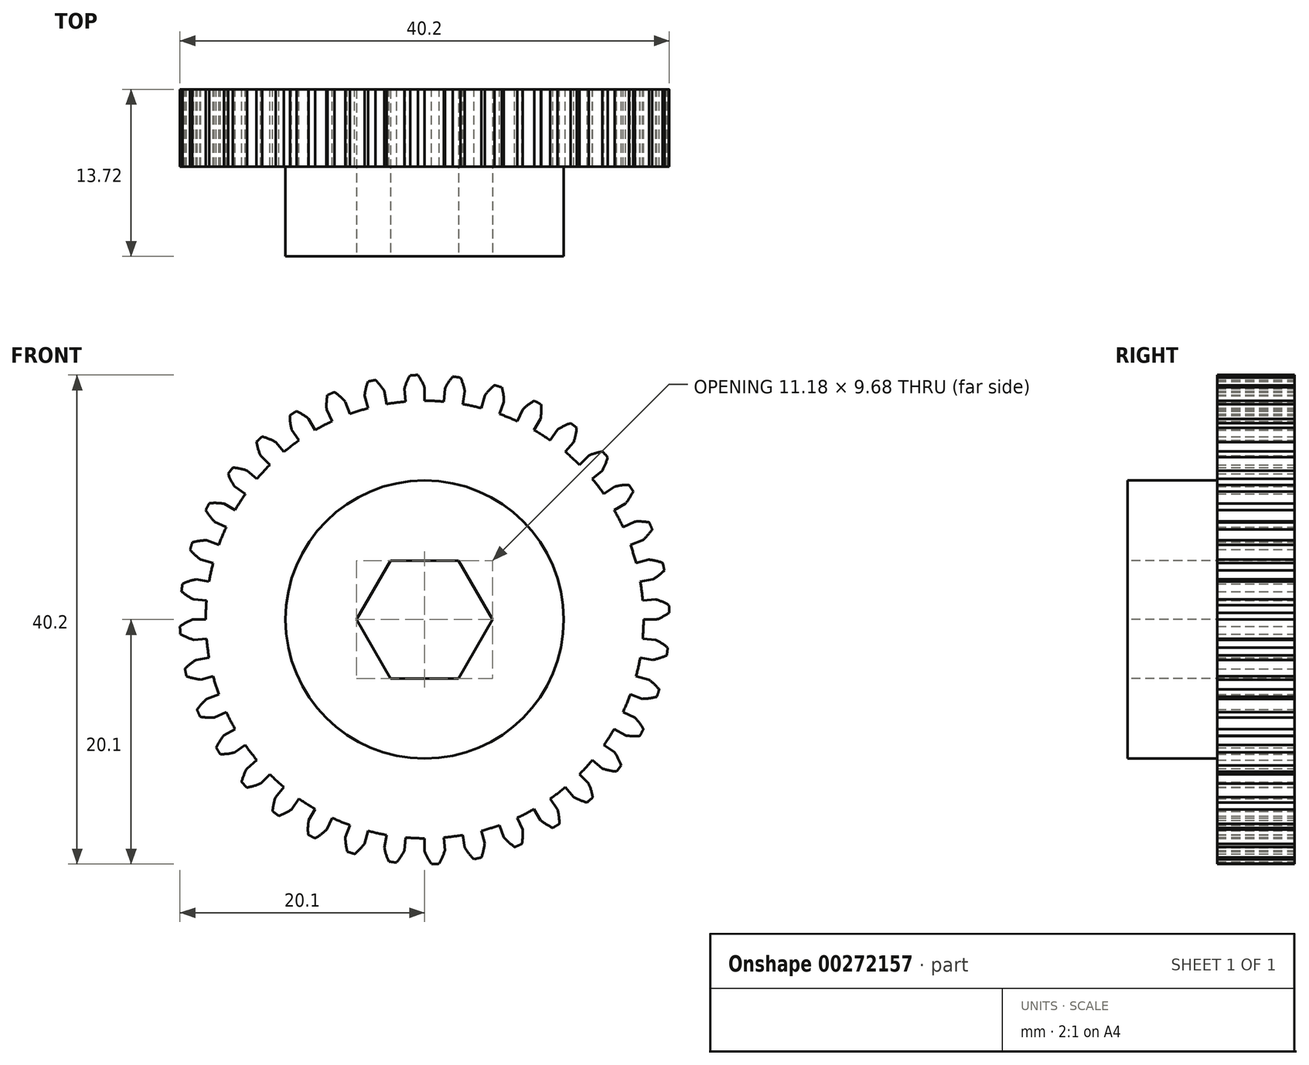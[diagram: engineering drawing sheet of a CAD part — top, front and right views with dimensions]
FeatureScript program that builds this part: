
annotation { "Feature Type Name" : "Feature", "Feature Type Description" : "" }
export const myFeature = defineFeature(function(context is Context, id is Id, definition is map)
    precondition{}
    {
        {
            var Q0;
            Q0=qCreatedBy(makeId("Front.planeOp"),FACE);
            var sketch = newSketch(context, id + "F0", { "sketchPlane" : qUnion([Q0])});
            skArc(sketch, "E0", {"start": v(4.65, 17.37) * mm, "mid": v(-6.88, -16.61) * mm, "end": v(9, 15.57) * mm});
            skLineSegment(sketch, "E1", {"start": v(0, 17.98) * mm, "end": v(0, 19.05) * mm});
            skLineSegment(sketch, "E2", {"start": v(0, 0) * mm, "end": v(-0.88, 20.08) * mm, "construction": true});
            skArc(sketch, "E3.trimOffspring", {"start": v(-0.56, 20.1) * mm, "mid": v(-0.72, 20.1) * mm, "end": v(-0.88, 20.08) * mm});
            skArc(sketch, "E4.trimOffspring", {"start": v(0, 19.05) * mm, "mid": v(-0.25, 19.6) * mm, "end": v(-0.56, 20.1) * mm});
            skLineSegment(sketch, "E5.MirrorCS", {"start": v(-1.57, 17.91) * mm, "end": v(-1.66, 18.98) * mm});
            skArc(sketch, "E6.MirrorCS", {"start": v(-1.66, 18.98) * mm, "mid": v(-1.46, 19.54) * mm, "end": v(-1.2, 20.07) * mm});
            skArc(sketch, "E7.MirrorCS", {"start": v(-1.2, 20.07) * mm, "mid": v(-1.03, 20.08) * mm, "end": v(-0.88, 20.08) * mm});
            skLineSegment(sketch, "E8.1.0", {"start": v(-4.65, 17.37) * mm, "end": v(-4.93, 18.4) * mm});
            skArc(sketch, "E8.1.1", {"start": v(-3.3, 18.76) * mm, "mid": v(-3.65, 19.25) * mm, "end": v(-4.04, 19.7) * mm});
            skLineSegment(sketch, "E8.1.2", {"start": v(-3.12, 17.7) * mm, "end": v(-3.3, 18.76) * mm});
            skArc(sketch, "E8.1.3", {"start": v(-4.93, 18.4) * mm, "mid": v(-4.83, 18.99) * mm, "end": v(-4.66, 19.56) * mm});
            skArc(sketch, "E8.1.4", {"start": v(-4.66, 19.56) * mm, "mid": v(-4.5, 19.6) * mm, "end": v(-4.35, 19.63) * mm});
            skArc(sketch, "E8.1.5", {"start": v(-4.04, 19.7) * mm, "mid": v(-4.2, 19.66) * mm, "end": v(-4.35, 19.63) * mm});
            skLineSegment(sketch, "E8.2.0", {"start": v(-7.6, 16.3) * mm, "end": v(-8.05, 17.27) * mm});
            skArc(sketch, "E8.2.1", {"start": v(-6.52, 17.9) * mm, "mid": v(-6.93, 18.32) * mm, "end": v(-7.4, 18.7) * mm});
            skLineSegment(sketch, "E8.2.2", {"start": v(-6.15, 16.9) * mm, "end": v(-6.52, 17.9) * mm});
            skArc(sketch, "E8.2.3", {"start": v(-8.05, 17.27) * mm, "mid": v(-8.05, 17.86) * mm, "end": v(-7.98, 18.45) * mm});
            skArc(sketch, "E8.2.4", {"start": v(-7.98, 18.45) * mm, "mid": v(-7.84, 18.51) * mm, "end": v(-7.7, 18.57) * mm});
            skArc(sketch, "E8.2.5", {"start": v(-7.4, 18.7) * mm, "mid": v(-7.55, 18.63) * mm, "end": v(-7.7, 18.57) * mm});
            skLineSegment(sketch, "E8.3.0", {"start": v(-10.31, 14.73) * mm, "end": v(-10.93, 15.6) * mm});
            skArc(sketch, "E8.3.1", {"start": v(-9.52, 16.5) * mm, "mid": v(-10, 16.84) * mm, "end": v(-10.53, 17.12) * mm});
            skLineSegment(sketch, "E8.3.2", {"start": v(-9, 15.57) * mm, "end": v(-9.52, 16.5) * mm});
            skArc(sketch, "E8.3.3", {"start": v(-10.93, 15.6) * mm, "mid": v(-11.03, 16.19) * mm, "end": v(-11.07, 16.78) * mm});
            skArc(sketch, "E8.3.4", {"start": v(-11.07, 16.78) * mm, "mid": v(-10.93, 16.87) * mm, "end": v(-10.8, 16.96) * mm});
            skArc(sketch, "E8.3.5", {"start": v(-10.53, 17.12) * mm, "mid": v(-10.67, 17.04) * mm, "end": v(-10.8, 16.96) * mm});
            skLineSegment(sketch, "E8.4.0", {"start": v(-12.72, 12.72) * mm, "end": v(-13.47, 13.47) * mm});
            skArc(sketch, "E8.4.1", {"start": v(-12.25, 14.6) * mm, "mid": v(-12.78, 14.85) * mm, "end": v(-13.35, 15.03) * mm});
            skLineSegment(sketch, "E8.4.2", {"start": v(-11.56, 13.78) * mm, "end": v(-12.25, 14.6) * mm});
            skArc(sketch, "E8.4.3", {"start": v(-13.47, 13.47) * mm, "mid": v(-13.68, 14.03) * mm, "end": v(-13.81, 14.6) * mm});
            skArc(sketch, "E8.4.4", {"start": v(-13.81, 14.6) * mm, "mid": v(-13.7, 14.72) * mm, "end": v(-13.58, 14.82) * mm});
            skArc(sketch, "E8.4.5", {"start": v(-13.35, 15.03) * mm, "mid": v(-13.47, 14.93) * mm, "end": v(-13.58, 14.82) * mm});
            skLineSegment(sketch, "E8.5.0", {"start": v(-14.73, 10.31) * mm, "end": v(-15.6, 10.93) * mm});
            skArc(sketch, "E8.5.1", {"start": v(-14.6, 12.25) * mm, "mid": v(-15.17, 12.4) * mm, "end": v(-15.76, 12.49) * mm});
            skLineSegment(sketch, "E8.5.2", {"start": v(-13.78, 11.56) * mm, "end": v(-14.6, 12.25) * mm});
            skArc(sketch, "E8.5.3", {"start": v(-15.6, 10.93) * mm, "mid": v(-15.9, 11.44) * mm, "end": v(-16.14, 11.99) * mm});
            skArc(sketch, "E8.5.4", {"start": v(-16.14, 11.99) * mm, "mid": v(-16.05, 12.11) * mm, "end": v(-15.95, 12.24) * mm});
            skArc(sketch, "E8.5.5", {"start": v(-15.76, 12.49) * mm, "mid": v(-15.85, 12.36) * mm, "end": v(-15.95, 12.24) * mm});
            skLineSegment(sketch, "E8.6.0", {"start": v(-16.3, 7.6) * mm, "end": v(-17.27, 8.05) * mm});
            skArc(sketch, "E8.6.1", {"start": v(-16.5, 9.53) * mm, "mid": v(-17.09, 9.58) * mm, "end": v(-17.68, 9.56) * mm});
            skLineSegment(sketch, "E8.6.2", {"start": v(-15.57, 9) * mm, "end": v(-16.5, 9.53) * mm});
            skArc(sketch, "E8.6.3", {"start": v(-17.27, 8.05) * mm, "mid": v(-17.65, 8.5) * mm, "end": v(-17.98, 9) * mm});
            skArc(sketch, "E8.6.4", {"start": v(-17.98, 9) * mm, "mid": v(-17.9, 9.14) * mm, "end": v(-17.83, 9.28) * mm});
            skArc(sketch, "E8.6.5", {"start": v(-17.68, 9.56) * mm, "mid": v(-17.76, 9.42) * mm, "end": v(-17.83, 9.28) * mm});
            skLineSegment(sketch, "E8.7.0", {"start": v(-17.37, 4.65) * mm, "end": v(-18.4, 4.93) * mm});
            skArc(sketch, "E8.7.1", {"start": v(-17.9, 6.52) * mm, "mid": v(-18.5, 6.47) * mm, "end": v(-19.08, 6.35) * mm});
            skLineSegment(sketch, "E8.7.2", {"start": v(-16.9, 6.15) * mm, "end": v(-17.9, 6.52) * mm});
            skArc(sketch, "E8.7.3", {"start": v(-18.4, 4.93) * mm, "mid": v(-18.86, 5.3) * mm, "end": v(-19.27, 5.74) * mm});
            skArc(sketch, "E8.7.4", {"start": v(-19.27, 5.74) * mm, "mid": v(-19.22, 5.9) * mm, "end": v(-19.17, 6.05) * mm});
            skArc(sketch, "E8.7.5", {"start": v(-19.08, 6.35) * mm, "mid": v(-19.13, 6.2) * mm, "end": v(-19.17, 6.05) * mm});
            skLineSegment(sketch, "E8.8.0", {"start": v(-17.91, 1.57) * mm, "end": v(-18.98, 1.66) * mm});
            skArc(sketch, "E8.8.1", {"start": v(-18.76, 3.3) * mm, "mid": v(-19.34, 3.16) * mm, "end": v(-19.89, 2.94) * mm});
            skLineSegment(sketch, "E8.8.2", {"start": v(-17.7, 3.12) * mm, "end": v(-18.76, 3.3) * mm});
            skArc(sketch, "E8.8.3", {"start": v(-18.98, 1.66) * mm, "mid": v(-19.5, 1.95) * mm, "end": v(-19.97, 2.31) * mm});
            skArc(sketch, "E8.8.4", {"start": v(-19.97, 2.31) * mm, "mid": v(-19.95, 2.47) * mm, "end": v(-19.93, 2.62) * mm});
            skArc(sketch, "E8.8.5", {"start": v(-19.89, 2.94) * mm, "mid": v(-19.91, 2.78) * mm, "end": v(-19.93, 2.62) * mm});
            skLineSegment(sketch, "E8.9.0", {"start": v(-17.91, -1.57) * mm, "end": v(-18.98, -1.66) * mm});
            skArc(sketch, "E8.9.1", {"start": v(-19.05, 0) * mm, "mid": v(-19.6, -0.25) * mm, "end": v(-20.1, -0.56) * mm});
            skLineSegment(sketch, "E8.9.2", {"start": v(-17.98, 0) * mm, "end": v(-19.05, 0) * mm});
            skArc(sketch, "E8.9.3", {"start": v(-18.98, -1.66) * mm, "mid": v(-19.54, -1.46) * mm, "end": v(-20.07, -1.2) * mm});
            skArc(sketch, "E8.9.4", {"start": v(-20.07, -1.2) * mm, "mid": v(-20.08, -1.03) * mm, "end": v(-20.08, -0.88) * mm});
            skArc(sketch, "E8.9.5", {"start": v(-20.1, -0.56) * mm, "mid": v(-20.1, -0.72) * mm, "end": v(-20.08, -0.88) * mm});
            skLineSegment(sketch, "E8.10.0", {"start": v(-17.37, -4.65) * mm, "end": v(-18.4, -4.93) * mm});
            skArc(sketch, "E8.10.1", {"start": v(-18.76, -3.3) * mm, "mid": v(-19.25, -3.65) * mm, "end": v(-19.7, -4.04) * mm});
            skLineSegment(sketch, "E8.10.2", {"start": v(-17.7, -3.12) * mm, "end": v(-18.76, -3.3) * mm});
            skArc(sketch, "E8.10.3", {"start": v(-18.4, -4.93) * mm, "mid": v(-18.99, -4.83) * mm, "end": v(-19.56, -4.66) * mm});
            skArc(sketch, "E8.10.4", {"start": v(-19.56, -4.66) * mm, "mid": v(-19.6, -4.5) * mm, "end": v(-19.63, -4.35) * mm});
            skArc(sketch, "E8.10.5", {"start": v(-19.7, -4.04) * mm, "mid": v(-19.66, -4.2) * mm, "end": v(-19.63, -4.35) * mm});
            skLineSegment(sketch, "E8.11.0", {"start": v(-16.3, -7.6) * mm, "end": v(-17.27, -8.05) * mm});
            skArc(sketch, "E8.11.1", {"start": v(-17.9, -6.52) * mm, "mid": v(-18.32, -6.93) * mm, "end": v(-18.7, -7.4) * mm});
            skLineSegment(sketch, "E8.11.2", {"start": v(-16.9, -6.15) * mm, "end": v(-17.9, -6.52) * mm});
            skArc(sketch, "E8.11.3", {"start": v(-17.27, -8.05) * mm, "mid": v(-17.86, -8.05) * mm, "end": v(-18.45, -7.98) * mm});
            skArc(sketch, "E8.11.4", {"start": v(-18.45, -7.98) * mm, "mid": v(-18.51, -7.84) * mm, "end": v(-18.57, -7.7) * mm});
            skArc(sketch, "E8.11.5", {"start": v(-18.7, -7.4) * mm, "mid": v(-18.63, -7.55) * mm, "end": v(-18.57, -7.7) * mm});
            skLineSegment(sketch, "E8.12.0", {"start": v(-14.73, -10.31) * mm, "end": v(-15.6, -10.93) * mm});
            skArc(sketch, "E8.12.1", {"start": v(-16.5, -9.52) * mm, "mid": v(-16.84, -10) * mm, "end": v(-17.12, -10.53) * mm});
            skLineSegment(sketch, "E8.12.2", {"start": v(-15.57, -9) * mm, "end": v(-16.5, -9.52) * mm});
            skArc(sketch, "E8.12.3", {"start": v(-15.6, -10.93) * mm, "mid": v(-16.19, -11.03) * mm, "end": v(-16.78, -11.07) * mm});
            skArc(sketch, "E8.12.4", {"start": v(-16.78, -11.07) * mm, "mid": v(-16.87, -10.93) * mm, "end": v(-16.96, -10.8) * mm});
            skArc(sketch, "E8.12.5", {"start": v(-17.12, -10.53) * mm, "mid": v(-17.04, -10.67) * mm, "end": v(-16.96, -10.8) * mm});
            skLineSegment(sketch, "E8.13.0", {"start": v(-12.72, -12.72) * mm, "end": v(-13.47, -13.47) * mm});
            skArc(sketch, "E8.13.1", {"start": v(-14.6, -12.25) * mm, "mid": v(-14.85, -12.78) * mm, "end": v(-15.03, -13.35) * mm});
            skLineSegment(sketch, "E8.13.2", {"start": v(-13.78, -11.56) * mm, "end": v(-14.6, -12.25) * mm});
            skArc(sketch, "E8.13.3", {"start": v(-13.47, -13.47) * mm, "mid": v(-14.03, -13.68) * mm, "end": v(-14.6, -13.81) * mm});
            skArc(sketch, "E8.13.4", {"start": v(-14.6, -13.81) * mm, "mid": v(-14.72, -13.7) * mm, "end": v(-14.82, -13.58) * mm});
            skArc(sketch, "E8.13.5", {"start": v(-15.03, -13.35) * mm, "mid": v(-14.93, -13.47) * mm, "end": v(-14.82, -13.58) * mm});
            skLineSegment(sketch, "E8.14.0", {"start": v(-10.31, -14.73) * mm, "end": v(-10.93, -15.6) * mm});
            skArc(sketch, "E8.14.1", {"start": v(-12.25, -14.6) * mm, "mid": v(-12.4, -15.17) * mm, "end": v(-12.49, -15.76) * mm});
            skLineSegment(sketch, "E8.14.2", {"start": v(-11.56, -13.78) * mm, "end": v(-12.25, -14.6) * mm});
            skArc(sketch, "E8.14.3", {"start": v(-10.93, -15.6) * mm, "mid": v(-11.44, -15.9) * mm, "end": v(-11.99, -16.14) * mm});
            skArc(sketch, "E8.14.4", {"start": v(-11.99, -16.14) * mm, "mid": v(-12.11, -16.05) * mm, "end": v(-12.24, -15.95) * mm});
            skArc(sketch, "E8.14.5", {"start": v(-12.49, -15.76) * mm, "mid": v(-12.36, -15.85) * mm, "end": v(-12.24, -15.95) * mm});
            skLineSegment(sketch, "E8.15.0", {"start": v(-7.6, -16.3) * mm, "end": v(-8.05, -17.27) * mm});
            skArc(sketch, "E8.15.1", {"start": v(-9.53, -16.5) * mm, "mid": v(-9.58, -17.09) * mm, "end": v(-9.56, -17.68) * mm});
            skLineSegment(sketch, "E8.15.2", {"start": v(-9, -15.57) * mm, "end": v(-9.53, -16.5) * mm});
            skArc(sketch, "E8.15.3", {"start": v(-8.05, -17.27) * mm, "mid": v(-8.5, -17.65) * mm, "end": v(-9, -17.98) * mm});
            skArc(sketch, "E8.15.4", {"start": v(-9, -17.98) * mm, "mid": v(-9.14, -17.9) * mm, "end": v(-9.28, -17.83) * mm});
            skArc(sketch, "E8.15.5", {"start": v(-9.56, -17.68) * mm, "mid": v(-9.42, -17.76) * mm, "end": v(-9.28, -17.83) * mm});
            skLineSegment(sketch, "E8.16.0", {"start": v(-4.65, -17.37) * mm, "end": v(-4.93, -18.4) * mm});
            skArc(sketch, "E8.16.1", {"start": v(-6.52, -17.9) * mm, "mid": v(-6.47, -18.5) * mm, "end": v(-6.35, -19.08) * mm});
            skLineSegment(sketch, "E8.16.2", {"start": v(-6.15, -16.9) * mm, "end": v(-6.52, -17.9) * mm});
            skArc(sketch, "E8.16.3", {"start": v(-4.93, -18.4) * mm, "mid": v(-5.3, -18.86) * mm, "end": v(-5.74, -19.27) * mm});
            skArc(sketch, "E8.16.4", {"start": v(-5.74, -19.27) * mm, "mid": v(-5.9, -19.22) * mm, "end": v(-6.05, -19.17) * mm});
            skArc(sketch, "E8.16.5", {"start": v(-6.35, -19.08) * mm, "mid": v(-6.2, -19.13) * mm, "end": v(-6.05, -19.17) * mm});
            skLineSegment(sketch, "E8.17.0", {"start": v(-1.57, -17.91) * mm, "end": v(-1.66, -18.98) * mm});
            skArc(sketch, "E8.17.1", {"start": v(-3.3, -18.76) * mm, "mid": v(-3.16, -19.34) * mm, "end": v(-2.94, -19.89) * mm});
            skLineSegment(sketch, "E8.17.2", {"start": v(-3.12, -17.7) * mm, "end": v(-3.3, -18.76) * mm});
            skArc(sketch, "E8.17.3", {"start": v(-1.66, -18.98) * mm, "mid": v(-1.95, -19.5) * mm, "end": v(-2.31, -19.97) * mm});
            skArc(sketch, "E8.17.4", {"start": v(-2.31, -19.97) * mm, "mid": v(-2.47, -19.95) * mm, "end": v(-2.62, -19.93) * mm});
            skArc(sketch, "E8.17.5", {"start": v(-2.94, -19.89) * mm, "mid": v(-2.78, -19.91) * mm, "end": v(-2.62, -19.93) * mm});
            skLineSegment(sketch, "E8.18.0", {"start": v(1.57, -17.91) * mm, "end": v(1.66, -18.98) * mm});
            skArc(sketch, "E8.18.1", {"start": v(0, -19.05) * mm, "mid": v(0.25, -19.6) * mm, "end": v(0.56, -20.1) * mm});
            skLineSegment(sketch, "E8.18.2", {"start": v(0, -17.98) * mm, "end": v(0, -19.05) * mm});
            skArc(sketch, "E8.18.3", {"start": v(1.66, -18.98) * mm, "mid": v(1.46, -19.54) * mm, "end": v(1.2, -20.07) * mm});
            skArc(sketch, "E8.18.4", {"start": v(1.2, -20.07) * mm, "mid": v(1.03, -20.08) * mm, "end": v(0.88, -20.08) * mm});
            skArc(sketch, "E8.18.5", {"start": v(0.56, -20.1) * mm, "mid": v(0.72, -20.1) * mm, "end": v(0.88, -20.08) * mm});
            skLineSegment(sketch, "E8.19.0", {"start": v(4.65, -17.37) * mm, "end": v(4.93, -18.4) * mm});
            skArc(sketch, "E8.19.1", {"start": v(3.3, -18.76) * mm, "mid": v(3.65, -19.25) * mm, "end": v(4.04, -19.7) * mm});
            skLineSegment(sketch, "E8.19.2", {"start": v(3.12, -17.7) * mm, "end": v(3.3, -18.76) * mm});
            skArc(sketch, "E8.19.3", {"start": v(4.93, -18.4) * mm, "mid": v(4.83, -18.99) * mm, "end": v(4.66, -19.56) * mm});
            skArc(sketch, "E8.19.4", {"start": v(4.66, -19.56) * mm, "mid": v(4.5, -19.6) * mm, "end": v(4.35, -19.63) * mm});
            skArc(sketch, "E8.19.5", {"start": v(4.04, -19.7) * mm, "mid": v(4.2, -19.66) * mm, "end": v(4.35, -19.63) * mm});
            skLineSegment(sketch, "E8.20.0", {"start": v(7.6, -16.3) * mm, "end": v(8.05, -17.27) * mm});
            skArc(sketch, "E8.20.1", {"start": v(6.52, -17.9) * mm, "mid": v(6.93, -18.32) * mm, "end": v(7.4, -18.7) * mm});
            skLineSegment(sketch, "E8.20.2", {"start": v(6.15, -16.9) * mm, "end": v(6.52, -17.9) * mm});
            skArc(sketch, "E8.20.3", {"start": v(8.05, -17.27) * mm, "mid": v(8.05, -17.86) * mm, "end": v(7.98, -18.45) * mm});
            skArc(sketch, "E8.20.4", {"start": v(7.98, -18.45) * mm, "mid": v(7.84, -18.51) * mm, "end": v(7.7, -18.57) * mm});
            skArc(sketch, "E8.20.5", {"start": v(7.4, -18.7) * mm, "mid": v(7.55, -18.63) * mm, "end": v(7.7, -18.57) * mm});
            skLineSegment(sketch, "E8.21.0", {"start": v(10.31, -14.73) * mm, "end": v(10.93, -15.6) * mm});
            skArc(sketch, "E8.21.1", {"start": v(9.52, -16.5) * mm, "mid": v(10, -16.84) * mm, "end": v(10.53, -17.12) * mm});
            skLineSegment(sketch, "E8.21.2", {"start": v(9, -15.57) * mm, "end": v(9.53, -16.5) * mm});
            skArc(sketch, "E8.21.3", {"start": v(10.93, -15.6) * mm, "mid": v(11.03, -16.19) * mm, "end": v(11.07, -16.78) * mm});
            skArc(sketch, "E8.21.4", {"start": v(11.07, -16.78) * mm, "mid": v(10.93, -16.87) * mm, "end": v(10.8, -16.96) * mm});
            skArc(sketch, "E8.21.5", {"start": v(10.53, -17.12) * mm, "mid": v(10.67, -17.04) * mm, "end": v(10.8, -16.96) * mm});
            skLineSegment(sketch, "E8.22.0", {"start": v(12.72, -12.72) * mm, "end": v(13.47, -13.47) * mm});
            skArc(sketch, "E8.22.1", {"start": v(12.25, -14.6) * mm, "mid": v(12.78, -14.85) * mm, "end": v(13.35, -15.03) * mm});
            skLineSegment(sketch, "E8.22.2", {"start": v(11.56, -13.78) * mm, "end": v(12.25, -14.6) * mm});
            skArc(sketch, "E8.22.3", {"start": v(13.47, -13.47) * mm, "mid": v(13.68, -14.03) * mm, "end": v(13.81, -14.6) * mm});
            skArc(sketch, "E8.22.4", {"start": v(13.81, -14.6) * mm, "mid": v(13.7, -14.72) * mm, "end": v(13.58, -14.82) * mm});
            skArc(sketch, "E8.22.5", {"start": v(13.35, -15.03) * mm, "mid": v(13.47, -14.93) * mm, "end": v(13.58, -14.82) * mm});
            skLineSegment(sketch, "E8.23.0", {"start": v(14.73, -10.31) * mm, "end": v(15.6, -10.93) * mm});
            skArc(sketch, "E8.23.1", {"start": v(14.6, -12.25) * mm, "mid": v(15.17, -12.4) * mm, "end": v(15.76, -12.49) * mm});
            skLineSegment(sketch, "E8.23.2", {"start": v(13.78, -11.56) * mm, "end": v(14.6, -12.25) * mm});
            skArc(sketch, "E8.23.3", {"start": v(15.6, -10.93) * mm, "mid": v(15.9, -11.44) * mm, "end": v(16.14, -11.99) * mm});
            skArc(sketch, "E8.23.4", {"start": v(16.14, -11.99) * mm, "mid": v(16.05, -12.11) * mm, "end": v(15.95, -12.24) * mm});
            skArc(sketch, "E8.23.5", {"start": v(15.76, -12.49) * mm, "mid": v(15.85, -12.36) * mm, "end": v(15.95, -12.24) * mm});
            skLineSegment(sketch, "E8.24.0", {"start": v(16.3, -7.6) * mm, "end": v(17.27, -8.05) * mm});
            skArc(sketch, "E8.24.1", {"start": v(16.5, -9.53) * mm, "mid": v(17.09, -9.58) * mm, "end": v(17.68, -9.56) * mm});
            skLineSegment(sketch, "E8.24.2", {"start": v(15.57, -9) * mm, "end": v(16.5, -9.53) * mm});
            skArc(sketch, "E8.24.3", {"start": v(17.27, -8.05) * mm, "mid": v(17.65, -8.5) * mm, "end": v(17.98, -9) * mm});
            skArc(sketch, "E8.24.4", {"start": v(17.98, -9) * mm, "mid": v(17.9, -9.14) * mm, "end": v(17.83, -9.28) * mm});
            skArc(sketch, "E8.24.5", {"start": v(17.68, -9.56) * mm, "mid": v(17.76, -9.42) * mm, "end": v(17.83, -9.28) * mm});
            skLineSegment(sketch, "E8.25.0", {"start": v(17.37, -4.65) * mm, "end": v(18.4, -4.93) * mm});
            skArc(sketch, "E8.25.1", {"start": v(17.9, -6.52) * mm, "mid": v(18.5, -6.47) * mm, "end": v(19.08, -6.35) * mm});
            skLineSegment(sketch, "E8.25.2", {"start": v(16.9, -6.15) * mm, "end": v(17.9, -6.52) * mm});
            skArc(sketch, "E8.25.3", {"start": v(18.4, -4.93) * mm, "mid": v(18.86, -5.3) * mm, "end": v(19.27, -5.74) * mm});
            skArc(sketch, "E8.25.4", {"start": v(19.27, -5.74) * mm, "mid": v(19.22, -5.9) * mm, "end": v(19.17, -6.05) * mm});
            skArc(sketch, "E8.25.5", {"start": v(19.08, -6.35) * mm, "mid": v(19.13, -6.2) * mm, "end": v(19.17, -6.05) * mm});
            skLineSegment(sketch, "E8.26.0", {"start": v(17.91, -1.57) * mm, "end": v(18.98, -1.66) * mm});
            skArc(sketch, "E8.26.1", {"start": v(18.76, -3.3) * mm, "mid": v(19.34, -3.16) * mm, "end": v(19.89, -2.94) * mm});
            skLineSegment(sketch, "E8.26.2", {"start": v(17.7, -3.12) * mm, "end": v(18.76, -3.3) * mm});
            skArc(sketch, "E8.26.3", {"start": v(18.98, -1.66) * mm, "mid": v(19.5, -1.95) * mm, "end": v(19.97, -2.31) * mm});
            skArc(sketch, "E8.26.4", {"start": v(19.97, -2.31) * mm, "mid": v(19.95, -2.47) * mm, "end": v(19.93, -2.62) * mm});
            skArc(sketch, "E8.26.5", {"start": v(19.89, -2.94) * mm, "mid": v(19.91, -2.78) * mm, "end": v(19.93, -2.62) * mm});
            skLineSegment(sketch, "E8.27.0", {"start": v(17.91, 1.57) * mm, "end": v(18.98, 1.66) * mm});
            skArc(sketch, "E8.27.1", {"start": v(19.05, 0) * mm, "mid": v(19.6, 0.25) * mm, "end": v(20.1, 0.56) * mm});
            skLineSegment(sketch, "E8.27.2", {"start": v(17.98, 0) * mm, "end": v(19.05, 0) * mm});
            skArc(sketch, "E8.27.3", {"start": v(18.98, 1.66) * mm, "mid": v(19.54, 1.46) * mm, "end": v(20.07, 1.2) * mm});
            skArc(sketch, "E8.27.4", {"start": v(20.07, 1.2) * mm, "mid": v(20.08, 1.03) * mm, "end": v(20.08, 0.88) * mm});
            skArc(sketch, "E8.27.5", {"start": v(20.1, 0.56) * mm, "mid": v(20.1, 0.72) * mm, "end": v(20.08, 0.88) * mm});
            skLineSegment(sketch, "E8.28.0", {"start": v(17.37, 4.65) * mm, "end": v(18.4, 4.93) * mm});
            skArc(sketch, "E8.28.1", {"start": v(18.76, 3.3) * mm, "mid": v(19.25, 3.65) * mm, "end": v(19.7, 4.04) * mm});
            skLineSegment(sketch, "E8.28.2", {"start": v(17.7, 3.12) * mm, "end": v(18.76, 3.3) * mm});
            skArc(sketch, "E8.28.3", {"start": v(18.4, 4.93) * mm, "mid": v(18.99, 4.83) * mm, "end": v(19.56, 4.66) * mm});
            skArc(sketch, "E8.28.4", {"start": v(19.56, 4.66) * mm, "mid": v(19.6, 4.5) * mm, "end": v(19.63, 4.35) * mm});
            skArc(sketch, "E8.28.5", {"start": v(19.7, 4.04) * mm, "mid": v(19.66, 4.2) * mm, "end": v(19.63, 4.35) * mm});
            skLineSegment(sketch, "E8.29.0", {"start": v(16.3, 7.6) * mm, "end": v(17.27, 8.05) * mm});
            skArc(sketch, "E8.29.1", {"start": v(17.9, 6.52) * mm, "mid": v(18.32, 6.93) * mm, "end": v(18.7, 7.4) * mm});
            skLineSegment(sketch, "E8.29.2", {"start": v(16.9, 6.15) * mm, "end": v(17.9, 6.52) * mm});
            skArc(sketch, "E8.29.3", {"start": v(17.27, 8.05) * mm, "mid": v(17.86, 8.05) * mm, "end": v(18.45, 7.98) * mm});
            skArc(sketch, "E8.29.4", {"start": v(18.45, 7.98) * mm, "mid": v(18.51, 7.84) * mm, "end": v(18.57, 7.7) * mm});
            skArc(sketch, "E8.29.5", {"start": v(18.7, 7.4) * mm, "mid": v(18.63, 7.55) * mm, "end": v(18.57, 7.7) * mm});
            skLineSegment(sketch, "E8.30.0", {"start": v(14.73, 10.31) * mm, "end": v(15.6, 10.93) * mm});
            skArc(sketch, "E8.30.1", {"start": v(16.5, 9.52) * mm, "mid": v(16.84, 10) * mm, "end": v(17.12, 10.53) * mm});
            skLineSegment(sketch, "E8.30.2", {"start": v(15.57, 9) * mm, "end": v(16.5, 9.52) * mm});
            skArc(sketch, "E8.30.3", {"start": v(15.6, 10.93) * mm, "mid": v(16.19, 11.03) * mm, "end": v(16.78, 11.07) * mm});
            skArc(sketch, "E8.30.4", {"start": v(16.78, 11.07) * mm, "mid": v(16.87, 10.93) * mm, "end": v(16.96, 10.8) * mm});
            skArc(sketch, "E8.30.5", {"start": v(17.12, 10.53) * mm, "mid": v(17.04, 10.67) * mm, "end": v(16.96, 10.8) * mm});
            skLineSegment(sketch, "E8.31.0", {"start": v(12.72, 12.72) * mm, "end": v(13.47, 13.47) * mm});
            skArc(sketch, "E8.31.1", {"start": v(14.6, 12.25) * mm, "mid": v(14.85, 12.78) * mm, "end": v(15.03, 13.35) * mm});
            skLineSegment(sketch, "E8.31.2", {"start": v(13.78, 11.56) * mm, "end": v(14.6, 12.25) * mm});
            skArc(sketch, "E8.31.3", {"start": v(13.47, 13.47) * mm, "mid": v(14.03, 13.68) * mm, "end": v(14.6, 13.81) * mm});
            skArc(sketch, "E8.31.4", {"start": v(14.6, 13.81) * mm, "mid": v(14.72, 13.7) * mm, "end": v(14.82, 13.58) * mm});
            skArc(sketch, "E8.31.5", {"start": v(15.03, 13.35) * mm, "mid": v(14.93, 13.47) * mm, "end": v(14.82, 13.58) * mm});
            skLineSegment(sketch, "E8.32.0", {"start": v(10.31, 14.73) * mm, "end": v(10.93, 15.6) * mm});
            skArc(sketch, "E8.32.1", {"start": v(12.25, 14.6) * mm, "mid": v(12.4, 15.17) * mm, "end": v(12.49, 15.76) * mm});
            skLineSegment(sketch, "E8.32.2", {"start": v(11.56, 13.78) * mm, "end": v(12.25, 14.6) * mm});
            skArc(sketch, "E8.32.3", {"start": v(10.93, 15.6) * mm, "mid": v(11.44, 15.9) * mm, "end": v(11.99, 16.14) * mm});
            skArc(sketch, "E8.32.4", {"start": v(11.99, 16.14) * mm, "mid": v(12.11, 16.05) * mm, "end": v(12.24, 15.95) * mm});
            skArc(sketch, "E8.32.5", {"start": v(12.49, 15.76) * mm, "mid": v(12.36, 15.85) * mm, "end": v(12.24, 15.95) * mm});
            skLineSegment(sketch, "E8.33.0", {"start": v(7.6, 16.3) * mm, "end": v(8.05, 17.27) * mm});
            skArc(sketch, "E8.33.1", {"start": v(9.53, 16.5) * mm, "mid": v(9.58, 17.09) * mm, "end": v(9.56, 17.68) * mm});
            skLineSegment(sketch, "E8.33.2", {"start": v(9, 15.57) * mm, "end": v(9.52, 16.5) * mm});
            skArc(sketch, "E8.33.3", {"start": v(8.05, 17.27) * mm, "mid": v(8.5, 17.65) * mm, "end": v(9, 17.98) * mm});
            skArc(sketch, "E8.33.4", {"start": v(9, 17.98) * mm, "mid": v(9.14, 17.9) * mm, "end": v(9.28, 17.83) * mm});
            skArc(sketch, "E8.33.5", {"start": v(9.56, 17.68) * mm, "mid": v(9.42, 17.76) * mm, "end": v(9.28, 17.83) * mm});
            skLineSegment(sketch, "E8.34.0", {"start": v(4.65, 17.37) * mm, "end": v(4.93, 18.4) * mm});
            skArc(sketch, "E8.34.1", {"start": v(6.52, 17.9) * mm, "mid": v(6.47, 18.5) * mm, "end": v(6.35, 19.08) * mm});
            skLineSegment(sketch, "E8.34.2", {"start": v(6.15, 16.9) * mm, "end": v(6.52, 17.9) * mm});
            skArc(sketch, "E8.34.3", {"start": v(4.93, 18.4) * mm, "mid": v(5.3, 18.86) * mm, "end": v(5.74, 19.27) * mm});
            skArc(sketch, "E8.34.4", {"start": v(5.74, 19.27) * mm, "mid": v(5.9, 19.22) * mm, "end": v(6.05, 19.17) * mm});
            skArc(sketch, "E8.34.5", {"start": v(6.35, 19.08) * mm, "mid": v(6.2, 19.13) * mm, "end": v(6.05, 19.17) * mm});
            skLineSegment(sketch, "E8.35.0", {"start": v(1.57, 17.91) * mm, "end": v(1.66, 18.98) * mm});
            skArc(sketch, "E8.35.1", {"start": v(3.3, 18.76) * mm, "mid": v(3.16, 19.34) * mm, "end": v(2.94, 19.89) * mm});
            skLineSegment(sketch, "E8.35.2", {"start": v(3.12, 17.7) * mm, "end": v(3.3, 18.76) * mm});
            skArc(sketch, "E8.35.3", {"start": v(1.66, 18.98) * mm, "mid": v(1.95, 19.5) * mm, "end": v(2.31, 19.97) * mm});
            skArc(sketch, "E8.35.4", {"start": v(2.31, 19.97) * mm, "mid": v(2.47, 19.95) * mm, "end": v(2.62, 19.93) * mm});
            skArc(sketch, "E8.35.5", {"start": v(2.94, 19.89) * mm, "mid": v(2.78, 19.91) * mm, "end": v(2.62, 19.93) * mm});
            skArc(sketch, "E9.trimOffspring", {"start": v(7.6, 16.3) * mm, "mid": v(6.88, 16.61) * mm, "end": v(6.15, 16.9) * mm});
            skSolve(sketch);
        }
        {
            var Q0;
            Q0=makeQuery(id+"F0.imprint","IMPRINT",FACE,{"disambiguationData":[TD([[makeQuery(id+"F0.imprint","IMPRINT",EDGE,{"derivedFrom":sQuery(id+"F0.wireOp",EDGE,"E8.33.0")}),-1.0]])]});
            var Q1;
            {var subQ1=sQuery(id+"F0.wireOp",EDGE,"E8.3.0");Q1=makeQuery(id+"F0.imprint","IMPRINT",FACE,{"disambiguationData":[TD([[makeQuery(id+"F0.imprint","IMPRINT",EDGE,{"derivedFrom":subQ1}),-1.0]])]});}
            var Q2;
            {var subQ1=sQuery(id+"F0.wireOp",EDGE,"E8.11.0");Q2=makeQuery(id+"F0.imprint","IMPRINT",FACE,{"disambiguationData":[TD([[makeQuery(id+"F0.imprint","IMPRINT",EDGE,{"derivedFrom":subQ1}),-1.0]])]});}
            var Q3;
            {var subQ1=sQuery(id+"F0.wireOp",EDGE,"E8.20.0");Q3=makeQuery(id+"F0.imprint","IMPRINT",FACE,{"disambiguationData":[TD([[makeQuery(id+"F0.imprint","IMPRINT",EDGE,{"derivedFrom":subQ1}),-1.0]])]});}
            var Q4;
            {var subQ1=sQuery(id+"F0.wireOp",EDGE,"E8.14.0");Q4=makeQuery(id+"F0.imprint","IMPRINT",FACE,{"disambiguationData":[TD([[makeQuery(id+"F0.imprint","IMPRINT",EDGE,{"derivedFrom":subQ1}),-1.0]])]});}
            var Q5;
            {var subQ1=sQuery(id+"F0.wireOp",EDGE,"E8.13.0");Q5=makeQuery(id+"F0.imprint","IMPRINT",FACE,{"disambiguationData":[TD([[makeQuery(id+"F0.imprint","IMPRINT",EDGE,{"derivedFrom":subQ1}),-1.0]])]});}
            var Q6;
            {var subQ1=sQuery(id+"F0.wireOp",EDGE,"E8.2.0");Q6=makeQuery(id+"F0.imprint","IMPRINT",FACE,{"disambiguationData":[TD([[makeQuery(id+"F0.imprint","IMPRINT",EDGE,{"derivedFrom":subQ1}),-1.0]])]});}
            var Q7;
            {var subQ0=sQuery(id+"F0.wireOp",EDGE,"E8.4.0");Q7=makeQuery(id+"F0.imprint","IMPRINT",FACE,{"disambiguationData":[TD([[makeQuery(id+"F0.imprint","IMPRINT",EDGE,{"derivedFrom":subQ0}),-1.0]])]});}
            var Q8;
            {var subQ1=sQuery(id+"F0.wireOp",EDGE,"E8.6.0");Q8=makeQuery(id+"F0.imprint","IMPRINT",FACE,{"disambiguationData":[TD([[makeQuery(id+"F0.imprint","IMPRINT",EDGE,{"derivedFrom":subQ1}),-1.0]])]});}
            var Q9;
            {var subQ1=sQuery(id+"F0.wireOp",EDGE,"E8.30.0");Q9=makeQuery(id+"F0.imprint","IMPRINT",FACE,{"disambiguationData":[TD([[makeQuery(id+"F0.imprint","IMPRINT",EDGE,{"derivedFrom":subQ1}),-1.0]])]});}
            var Q10;
            {var subQ1=sQuery(id+"F0.wireOp",EDGE,"E8.22.0");Q10=makeQuery(id+"F0.imprint","IMPRINT",FACE,{"disambiguationData":[TD([[makeQuery(id+"F0.imprint","IMPRINT",EDGE,{"derivedFrom":subQ1}),-1.0]])]});}
            var Q11;
            {var subQ0=sQuery(id+"F0.wireOp",EDGE,"E8.23.0");Q11=makeQuery(id+"F0.imprint","IMPRINT",FACE,{"disambiguationData":[TD([[makeQuery(id+"F0.imprint","IMPRINT",EDGE,{"derivedFrom":subQ0}),-1.0]])]});}
            var Q12;
            {var subQ1=sQuery(id+"F0.wireOp",EDGE,"E8.28.0");Q12=makeQuery(id+"F0.imprint","IMPRINT",FACE,{"disambiguationData":[TD([[makeQuery(id+"F0.imprint","IMPRINT",EDGE,{"derivedFrom":subQ1}),-1.0]])]});}
            var Q13;
            {var subQ1=sQuery(id+"F0.wireOp",EDGE,"E8.29.0");Q13=makeQuery(id+"F0.imprint","IMPRINT",FACE,{"disambiguationData":[TD([[makeQuery(id+"F0.imprint","IMPRINT",EDGE,{"derivedFrom":subQ1}),-1.0]])]});}
            var Q14;
            {var subQ0=sQuery(id+"F0.wireOp",EDGE,"E8.15.0");Q14=makeQuery(id+"F0.imprint","IMPRINT",FACE,{"disambiguationData":[TD([[makeQuery(id+"F0.imprint","IMPRINT",EDGE,{"derivedFrom":subQ0}),-1.0]])]});}
            var Q15;
            {var subQ1=sQuery(id+"F0.wireOp",EDGE,"E8.31.0");Q15=makeQuery(id+"F0.imprint","IMPRINT",FACE,{"disambiguationData":[TD([[makeQuery(id+"F0.imprint","IMPRINT",EDGE,{"derivedFrom":subQ1}),-1.0]])]});}
            var Q16;
            {var subQ1=sQuery(id+"F0.wireOp",EDGE,"E8.16.0");Q16=makeQuery(id+"F0.imprint","IMPRINT",FACE,{"disambiguationData":[TD([[makeQuery(id+"F0.imprint","IMPRINT",EDGE,{"derivedFrom":subQ1}),-1.0]])]});}
            var Q17;
            {var subQ1=sQuery(id+"F0.wireOp",EDGE,"E8.32.0");Q17=makeQuery(id+"F0.imprint","IMPRINT",FACE,{"disambiguationData":[TD([[makeQuery(id+"F0.imprint","IMPRINT",EDGE,{"derivedFrom":subQ1}),-1.0]])]});}
            var Q18;
            {var subQ1=sQuery(id+"F0.wireOp",EDGE,"E8.17.0");Q18=makeQuery(id+"F0.imprint","IMPRINT",FACE,{"disambiguationData":[TD([[makeQuery(id+"F0.imprint","IMPRINT",EDGE,{"derivedFrom":subQ1}),-1.0]])]});}
            var Q19;
            {var subQ1=sQuery(id+"F0.wireOp",EDGE,"E8.18.0");Q19=makeQuery(id+"F0.imprint","IMPRINT",FACE,{"disambiguationData":[TD([[makeQuery(id+"F0.imprint","IMPRINT",EDGE,{"derivedFrom":subQ1}),-1.0]])]});}
            var Q20;
            {var subQ0=sQuery(id+"F0.wireOp",EDGE,"E8.19.0");Q20=makeQuery(id+"F0.imprint","IMPRINT",FACE,{"disambiguationData":[TD([[makeQuery(id+"F0.imprint","IMPRINT",EDGE,{"derivedFrom":subQ0}),-1.0]])]});}
            var Q21;
            {var subQ0=sQuery(id+"F0.wireOp",EDGE,"E8.21.0");Q21=makeQuery(id+"F0.imprint","IMPRINT",FACE,{"disambiguationData":[TD([[makeQuery(id+"F0.imprint","IMPRINT",EDGE,{"derivedFrom":subQ0}),-1.0]])]});}
            var Q22;
            {var subQ1=sQuery(id+"F0.wireOp",EDGE,"E8.12.0");Q22=makeQuery(id+"F0.imprint","IMPRINT",FACE,{"disambiguationData":[TD([[makeQuery(id+"F0.imprint","IMPRINT",EDGE,{"derivedFrom":subQ1}),-1.0]])]});}
            var Q23;
            {var subQ1=sQuery(id+"F0.wireOp",EDGE,"E8.35.0");Q23=makeQuery(id+"F0.imprint","IMPRINT",FACE,{"disambiguationData":[TD([[makeQuery(id+"F0.imprint","IMPRINT",EDGE,{"derivedFrom":subQ1}),-1.0]])]});}
            var Q24;
            {var subQ0=sQuery(id+"F0.wireOp",EDGE,"E1");Q24=makeQuery(id+"F0.imprint","IMPRINT",FACE,{"disambiguationData":[TD([[makeQuery(id+"F0.imprint","IMPRINT",EDGE,{"derivedFrom":subQ0}),1.0]])]});}
            var Q25;
            {var subQ1=sQuery(id+"F0.wireOp",EDGE,"E8.1.0");Q25=makeQuery(id+"F0.imprint","IMPRINT",FACE,{"disambiguationData":[TD([[makeQuery(id+"F0.imprint","IMPRINT",EDGE,{"derivedFrom":subQ1}),-1.0]])]});}
            var Q26;
            {var subQ1=sQuery(id+"F0.wireOp",EDGE,"E8.5.0");Q26=makeQuery(id+"F0.imprint","IMPRINT",FACE,{"disambiguationData":[TD([[makeQuery(id+"F0.imprint","IMPRINT",EDGE,{"derivedFrom":subQ1}),-1.0]])]});}
            var Q27;
            {var subQ1=sQuery(id+"F0.wireOp",EDGE,"E8.7.0");Q27=makeQuery(id+"F0.imprint","IMPRINT",FACE,{"disambiguationData":[TD([[makeQuery(id+"F0.imprint","IMPRINT",EDGE,{"derivedFrom":subQ1}),-1.0]])]});}
            var Q28;
            {var subQ1=sQuery(id+"F0.wireOp",EDGE,"E8.8.0");Q28=makeQuery(id+"F0.imprint","IMPRINT",FACE,{"disambiguationData":[TD([[makeQuery(id+"F0.imprint","IMPRINT",EDGE,{"derivedFrom":subQ1}),-1.0]])]});}
            var Q29;
            {var subQ1=sQuery(id+"F0.wireOp",EDGE,"E8.25.0");Q29=makeQuery(id+"F0.imprint","IMPRINT",FACE,{"disambiguationData":[TD([[makeQuery(id+"F0.imprint","IMPRINT",EDGE,{"derivedFrom":subQ1}),-1.0]])]});}
            var Q30;
            {var subQ1=sQuery(id+"F0.wireOp",EDGE,"E8.9.0");Q30=makeQuery(id+"F0.imprint","IMPRINT",FACE,{"disambiguationData":[TD([[makeQuery(id+"F0.imprint","IMPRINT",EDGE,{"derivedFrom":subQ1}),-1.0]])]});}
            var Q31;
            {var subQ1=sQuery(id+"F0.wireOp",EDGE,"E8.10.0");Q31=makeQuery(id+"F0.imprint","IMPRINT",FACE,{"disambiguationData":[TD([[makeQuery(id+"F0.imprint","IMPRINT",EDGE,{"derivedFrom":subQ1}),-1.0]])]});}
            var Q32;
            {var subQ1=sQuery(id+"F0.wireOp",EDGE,"E8.27.0");Q32=makeQuery(id+"F0.imprint","IMPRINT",FACE,{"disambiguationData":[TD([[makeQuery(id+"F0.imprint","IMPRINT",EDGE,{"derivedFrom":subQ1}),-1.0]])]});}
            var Q33;
            {var subQ1=sQuery(id+"F0.wireOp",EDGE,"E8.26.0");Q33=makeQuery(id+"F0.imprint","IMPRINT",FACE,{"disambiguationData":[TD([[makeQuery(id+"F0.imprint","IMPRINT",EDGE,{"derivedFrom":subQ1}),-1.0]])]});}
            var Q34;
            {var subQ1=sQuery(id+"F0.wireOp",EDGE,"E8.24.0");Q34=makeQuery(id+"F0.imprint","IMPRINT",FACE,{"disambiguationData":[TD([[makeQuery(id+"F0.imprint","IMPRINT",EDGE,{"derivedFrom":subQ1}),-1.0]])]});}
            extrude(context, id + "F1", {"entities" : qUnion([Q0, Q1, Q2, Q3, Q4, Q5, Q6, Q7, Q8, Q9, Q10, Q11, Q12, Q13, Q14, Q15, Q16, Q17, Q18, Q19, Q20, Q21, Q22, Q23, Q24, Q25, Q26, Q27, Q28, Q29, Q30, Q31, Q32, Q33, Q34]), "depth" : 6.35 * mm});
        }
        {
            var Q0;
            Q0=makeQuery(id+"F1.opExtrude","CAP_FACE",FACE,{"disambiguationData":[OSD([sQuery(id+"F0.wireOp",EDGE,"E0"),sQuery(id+"F0.wireOp",EDGE,"E1"),sQuery(id+"F0.wireOp",EDGE,"E3.trimOffspring"),sQuery(id+"F0.wireOp",EDGE,"E4.trimOffspring"),sQuery(id+"F0.wireOp",EDGE,"E5.MirrorCS"),sQuery(id+"F0.wireOp",EDGE,"E6.MirrorCS"),sQuery(id+"F0.wireOp",EDGE,"E7.MirrorCS"),sQuery(id+"F0.wireOp",EDGE,"E8.1.0"),sQuery(id+"F0.wireOp",EDGE,"E8.1.1"),sQuery(id+"F0.wireOp",EDGE,"E8.1.2"),sQuery(id+"F0.wireOp",EDGE,"E8.1.3"),sQuery(id+"F0.wireOp",EDGE,"E8.1.4"),sQuery(id+"F0.wireOp",EDGE,"E8.1.5"),sQuery(id+"F0.wireOp",EDGE,"E8.2.0"),sQuery(id+"F0.wireOp",EDGE,"E8.2.1"),sQuery(id+"F0.wireOp",EDGE,"E8.2.2"),sQuery(id+"F0.wireOp",EDGE,"E8.2.3"),sQuery(id+"F0.wireOp",EDGE,"E8.2.4"),sQuery(id+"F0.wireOp",EDGE,"E8.2.5"),sQuery(id+"F0.wireOp",EDGE,"E8.3.0"),sQuery(id+"F0.wireOp",EDGE,"E8.3.1"),sQuery(id+"F0.wireOp",EDGE,"E8.3.2"),sQuery(id+"F0.wireOp",EDGE,"E8.3.3"),sQuery(id+"F0.wireOp",EDGE,"E8.3.4"),sQuery(id+"F0.wireOp",EDGE,"E8.3.5"),sQuery(id+"F0.wireOp",EDGE,"E8.4.0"),sQuery(id+"F0.wireOp",EDGE,"E8.4.1"),sQuery(id+"F0.wireOp",EDGE,"E8.4.2"),sQuery(id+"F0.wireOp",EDGE,"E8.4.3"),sQuery(id+"F0.wireOp",EDGE,"E8.4.4"),sQuery(id+"F0.wireOp",EDGE,"E8.4.5"),sQuery(id+"F0.wireOp",EDGE,"E8.5.0"),sQuery(id+"F0.wireOp",EDGE,"E8.5.1"),sQuery(id+"F0.wireOp",EDGE,"E8.5.2"),sQuery(id+"F0.wireOp",EDGE,"E8.5.3"),sQuery(id+"F0.wireOp",EDGE,"E8.5.4"),sQuery(id+"F0.wireOp",EDGE,"E8.5.5"),sQuery(id+"F0.wireOp",EDGE,"E8.6.0"),sQuery(id+"F0.wireOp",EDGE,"E8.6.1"),sQuery(id+"F0.wireOp",EDGE,"E8.6.2"),sQuery(id+"F0.wireOp",EDGE,"E8.6.3"),sQuery(id+"F0.wireOp",EDGE,"E8.6.4"),sQuery(id+"F0.wireOp",EDGE,"E8.6.5"),sQuery(id+"F0.wireOp",EDGE,"E8.7.0"),sQuery(id+"F0.wireOp",EDGE,"E8.7.1"),sQuery(id+"F0.wireOp",EDGE,"E8.7.2"),sQuery(id+"F0.wireOp",EDGE,"E8.7.3"),sQuery(id+"F0.wireOp",EDGE,"E8.7.4"),sQuery(id+"F0.wireOp",EDGE,"E8.7.5"),sQuery(id+"F0.wireOp",EDGE,"E8.8.0"),sQuery(id+"F0.wireOp",EDGE,"E8.8.1"),sQuery(id+"F0.wireOp",EDGE,"E8.8.2"),sQuery(id+"F0.wireOp",EDGE,"E8.8.3"),sQuery(id+"F0.wireOp",EDGE,"E8.8.4"),sQuery(id+"F0.wireOp",EDGE,"E8.8.5"),sQuery(id+"F0.wireOp",EDGE,"E8.9.0"),sQuery(id+"F0.wireOp",EDGE,"E8.9.1"),sQuery(id+"F0.wireOp",EDGE,"E8.9.2"),sQuery(id+"F0.wireOp",EDGE,"E8.9.3"),sQuery(id+"F0.wireOp",EDGE,"E8.9.4"),sQuery(id+"F0.wireOp",EDGE,"E8.9.5"),sQuery(id+"F0.wireOp",EDGE,"E8.10.0"),sQuery(id+"F0.wireOp",EDGE,"E8.10.1"),sQuery(id+"F0.wireOp",EDGE,"E8.10.2"),sQuery(id+"F0.wireOp",EDGE,"E8.10.3"),sQuery(id+"F0.wireOp",EDGE,"E8.10.4"),sQuery(id+"F0.wireOp",EDGE,"E8.10.5"),sQuery(id+"F0.wireOp",EDGE,"E8.11.0"),sQuery(id+"F0.wireOp",EDGE,"E8.11.1"),sQuery(id+"F0.wireOp",EDGE,"E8.11.2"),sQuery(id+"F0.wireOp",EDGE,"E8.11.3"),sQuery(id+"F0.wireOp",EDGE,"E8.11.4"),sQuery(id+"F0.wireOp",EDGE,"E8.11.5"),sQuery(id+"F0.wireOp",EDGE,"E8.12.0"),sQuery(id+"F0.wireOp",EDGE,"E8.12.1"),sQuery(id+"F0.wireOp",EDGE,"E8.12.2"),sQuery(id+"F0.wireOp",EDGE,"E8.12.3"),sQuery(id+"F0.wireOp",EDGE,"E8.12.4"),sQuery(id+"F0.wireOp",EDGE,"E8.12.5"),sQuery(id+"F0.wireOp",EDGE,"E8.13.0"),sQuery(id+"F0.wireOp",EDGE,"E8.13.1"),sQuery(id+"F0.wireOp",EDGE,"E8.13.2"),sQuery(id+"F0.wireOp",EDGE,"E8.13.3"),sQuery(id+"F0.wireOp",EDGE,"E8.13.4"),sQuery(id+"F0.wireOp",EDGE,"E8.13.5"),sQuery(id+"F0.wireOp",EDGE,"E8.14.0"),sQuery(id+"F0.wireOp",EDGE,"E8.14.1"),sQuery(id+"F0.wireOp",EDGE,"E8.14.2"),sQuery(id+"F0.wireOp",EDGE,"E8.14.3"),sQuery(id+"F0.wireOp",EDGE,"E8.14.4"),sQuery(id+"F0.wireOp",EDGE,"E8.14.5"),sQuery(id+"F0.wireOp",EDGE,"E8.15.0"),sQuery(id+"F0.wireOp",EDGE,"E8.15.1"),sQuery(id+"F0.wireOp",EDGE,"E8.15.2"),sQuery(id+"F0.wireOp",EDGE,"E8.15.3"),sQuery(id+"F0.wireOp",EDGE,"E8.15.4"),sQuery(id+"F0.wireOp",EDGE,"E8.15.5"),sQuery(id+"F0.wireOp",EDGE,"E8.16.0"),sQuery(id+"F0.wireOp",EDGE,"E8.16.1"),sQuery(id+"F0.wireOp",EDGE,"E8.16.2"),sQuery(id+"F0.wireOp",EDGE,"E8.16.3"),sQuery(id+"F0.wireOp",EDGE,"E8.16.4"),sQuery(id+"F0.wireOp",EDGE,"E8.16.5"),sQuery(id+"F0.wireOp",EDGE,"E8.17.0"),sQuery(id+"F0.wireOp",EDGE,"E8.17.1"),sQuery(id+"F0.wireOp",EDGE,"E8.17.2"),sQuery(id+"F0.wireOp",EDGE,"E8.17.3"),sQuery(id+"F0.wireOp",EDGE,"E8.17.4"),sQuery(id+"F0.wireOp",EDGE,"E8.17.5"),sQuery(id+"F0.wireOp",EDGE,"E8.18.0"),sQuery(id+"F0.wireOp",EDGE,"E8.18.1"),sQuery(id+"F0.wireOp",EDGE,"E8.18.2"),sQuery(id+"F0.wireOp",EDGE,"E8.18.3"),sQuery(id+"F0.wireOp",EDGE,"E8.18.4"),sQuery(id+"F0.wireOp",EDGE,"E8.18.5"),sQuery(id+"F0.wireOp",EDGE,"E8.19.0"),sQuery(id+"F0.wireOp",EDGE,"E8.19.1"),sQuery(id+"F0.wireOp",EDGE,"E8.19.2"),sQuery(id+"F0.wireOp",EDGE,"E8.19.3"),sQuery(id+"F0.wireOp",EDGE,"E8.19.4"),sQuery(id+"F0.wireOp",EDGE,"E8.19.5"),sQuery(id+"F0.wireOp",EDGE,"E8.20.0"),sQuery(id+"F0.wireOp",EDGE,"E8.20.1"),sQuery(id+"F0.wireOp",EDGE,"E8.20.2"),sQuery(id+"F0.wireOp",EDGE,"E8.20.3"),sQuery(id+"F0.wireOp",EDGE,"E8.20.4"),sQuery(id+"F0.wireOp",EDGE,"E8.20.5"),sQuery(id+"F0.wireOp",EDGE,"E8.21.0"),sQuery(id+"F0.wireOp",EDGE,"E8.21.1"),sQuery(id+"F0.wireOp",EDGE,"E8.21.2"),sQuery(id+"F0.wireOp",EDGE,"E8.21.3"),sQuery(id+"F0.wireOp",EDGE,"E8.21.4"),sQuery(id+"F0.wireOp",EDGE,"E8.21.5"),sQuery(id+"F0.wireOp",EDGE,"E8.22.0"),sQuery(id+"F0.wireOp",EDGE,"E8.22.1"),sQuery(id+"F0.wireOp",EDGE,"E8.22.2"),sQuery(id+"F0.wireOp",EDGE,"E8.22.3"),sQuery(id+"F0.wireOp",EDGE,"E8.22.4"),sQuery(id+"F0.wireOp",EDGE,"E8.22.5"),sQuery(id+"F0.wireOp",EDGE,"E8.23.0"),sQuery(id+"F0.wireOp",EDGE,"E8.23.1"),sQuery(id+"F0.wireOp",EDGE,"E8.23.2"),sQuery(id+"F0.wireOp",EDGE,"E8.23.3"),sQuery(id+"F0.wireOp",EDGE,"E8.23.4"),sQuery(id+"F0.wireOp",EDGE,"E8.23.5"),sQuery(id+"F0.wireOp",EDGE,"E8.24.0"),sQuery(id+"F0.wireOp",EDGE,"E8.24.1"),sQuery(id+"F0.wireOp",EDGE,"E8.24.2"),sQuery(id+"F0.wireOp",EDGE,"E8.24.3"),sQuery(id+"F0.wireOp",EDGE,"E8.24.4"),sQuery(id+"F0.wireOp",EDGE,"E8.24.5"),sQuery(id+"F0.wireOp",EDGE,"E8.25.0"),sQuery(id+"F0.wireOp",EDGE,"E8.25.1"),sQuery(id+"F0.wireOp",EDGE,"E8.25.2"),sQuery(id+"F0.wireOp",EDGE,"E8.25.3"),sQuery(id+"F0.wireOp",EDGE,"E8.25.4"),sQuery(id+"F0.wireOp",EDGE,"E8.25.5"),sQuery(id+"F0.wireOp",EDGE,"E8.26.0"),sQuery(id+"F0.wireOp",EDGE,"E8.26.1"),sQuery(id+"F0.wireOp",EDGE,"E8.26.2"),sQuery(id+"F0.wireOp",EDGE,"E8.26.3"),sQuery(id+"F0.wireOp",EDGE,"E8.26.4"),sQuery(id+"F0.wireOp",EDGE,"E8.26.5"),sQuery(id+"F0.wireOp",EDGE,"E8.27.0"),sQuery(id+"F0.wireOp",EDGE,"E8.27.1"),sQuery(id+"F0.wireOp",EDGE,"E8.27.2"),sQuery(id+"F0.wireOp",EDGE,"E8.27.3"),sQuery(id+"F0.wireOp",EDGE,"E8.27.4"),sQuery(id+"F0.wireOp",EDGE,"E8.27.5"),sQuery(id+"F0.wireOp",EDGE,"E8.28.0"),sQuery(id+"F0.wireOp",EDGE,"E8.28.1"),sQuery(id+"F0.wireOp",EDGE,"E8.28.2"),sQuery(id+"F0.wireOp",EDGE,"E8.28.3"),sQuery(id+"F0.wireOp",EDGE,"E8.28.4"),sQuery(id+"F0.wireOp",EDGE,"E8.28.5"),sQuery(id+"F0.wireOp",EDGE,"E8.29.0"),sQuery(id+"F0.wireOp",EDGE,"E8.29.1"),sQuery(id+"F0.wireOp",EDGE,"E8.29.2"),sQuery(id+"F0.wireOp",EDGE,"E8.29.3"),sQuery(id+"F0.wireOp",EDGE,"E8.29.4"),sQuery(id+"F0.wireOp",EDGE,"E8.29.5"),sQuery(id+"F0.wireOp",EDGE,"E8.30.0"),sQuery(id+"F0.wireOp",EDGE,"E8.30.1"),sQuery(id+"F0.wireOp",EDGE,"E8.30.2"),sQuery(id+"F0.wireOp",EDGE,"E8.30.3"),sQuery(id+"F0.wireOp",EDGE,"E8.30.4"),sQuery(id+"F0.wireOp",EDGE,"E8.30.5"),sQuery(id+"F0.wireOp",EDGE,"E8.31.0"),sQuery(id+"F0.wireOp",EDGE,"E8.31.1"),sQuery(id+"F0.wireOp",EDGE,"E8.31.2"),sQuery(id+"F0.wireOp",EDGE,"E8.31.3"),sQuery(id+"F0.wireOp",EDGE,"E8.31.4"),sQuery(id+"F0.wireOp",EDGE,"E8.31.5"),sQuery(id+"F0.wireOp",EDGE,"E8.32.0"),sQuery(id+"F0.wireOp",EDGE,"E8.32.1"),sQuery(id+"F0.wireOp",EDGE,"E8.32.2"),sQuery(id+"F0.wireOp",EDGE,"E8.32.3"),sQuery(id+"F0.wireOp",EDGE,"E8.32.4"),sQuery(id+"F0.wireOp",EDGE,"E8.32.5"),sQuery(id+"F0.wireOp",EDGE,"E8.33.0"),sQuery(id+"F0.wireOp",EDGE,"E8.33.1"),sQuery(id+"F0.wireOp",EDGE,"E8.33.2"),sQuery(id+"F0.wireOp",EDGE,"E8.33.3"),sQuery(id+"F0.wireOp",EDGE,"E8.33.4"),sQuery(id+"F0.wireOp",EDGE,"E8.33.5"),sQuery(id+"F0.wireOp",EDGE,"E8.34.0"),sQuery(id+"F0.wireOp",EDGE,"E8.34.1"),sQuery(id+"F0.wireOp",EDGE,"E8.34.2"),sQuery(id+"F0.wireOp",EDGE,"E8.34.3"),sQuery(id+"F0.wireOp",EDGE,"E8.34.4"),sQuery(id+"F0.wireOp",EDGE,"E8.34.5"),sQuery(id+"F0.wireOp",EDGE,"E8.35.0"),sQuery(id+"F0.wireOp",EDGE,"E8.35.1"),sQuery(id+"F0.wireOp",EDGE,"E8.35.2"),sQuery(id+"F0.wireOp",EDGE,"E8.35.3"),sQuery(id+"F0.wireOp",EDGE,"E8.35.4"),sQuery(id+"F0.wireOp",EDGE,"E8.35.5"),sQuery(id+"F0.wireOp",EDGE,"E9.trimOffspring")])],"isStart":false});
            var sketch = newSketch(context, id + "F2", { "sketchPlane" : qUnion([Q0])});
            skCircle(sketch, "E10", {"center": v(0, 0) * mm, "radius": 11.43 * mm});
            skSolve(sketch);
        }
        {
            var Q0;
            Q0=qSketchRegion(id+"F2",true);
            extrude(context, id + "F3", {"entities" : qUnion([Q0]), "operationType" : NewBodyOperationType.ADD, "depth" : 7.37 * mm});
        }
        {
            var Q0;
            Q0=makeQuery(id+"F3.opExtrude","CAP_FACE",FACE,{"disambiguationData":[OSD([sQuery(id+"F2.wireOp",EDGE,"E10")])],"isStart":false});
            var sketch = newSketch(context, id + "F4", { "sketchPlane" : qUnion([Q0])});
            skCircle(sketch, "E11.cCircle", {"center": v(0, 0) * mm, "radius": 5.59 * mm, "construction": true});
            skLineSegment(sketch, "E11.0", {"start": v(5.59, 0) * mm, "end": v(2.8, -4.84) * mm});
            skLineSegment(sketch, "E11.1", {"start": v(2.8, -4.84) * mm, "end": v(-2.8, -4.84) * mm});
            skLineSegment(sketch, "E11.2", {"start": v(-2.8, -4.84) * mm, "end": v(-5.59, 0) * mm});
            skLineSegment(sketch, "E11.3", {"start": v(-5.59, 0) * mm, "end": v(-2.8, 4.84) * mm});
            skLineSegment(sketch, "E11.4", {"start": v(-2.8, 4.84) * mm, "end": v(2.8, 4.84) * mm});
            skLineSegment(sketch, "E11.5", {"start": v(2.8, 4.84) * mm, "end": v(5.59, 0) * mm});
            skSolve(sketch);
        }
        {
            var Q0;
            Q0=makeQuery(id+"F4.imprint","IMPRINT",FACE,{"disambiguationData":[TD([[makeQuery(id+"F4.imprint","IMPRINT",EDGE,{"derivedFrom":sQuery(id+"F4.wireOp",EDGE,"E11.0")}),-1.0]])]});
            extrude(context, id + "F5", {"entities" : qUnion([Q0]), "operationType" : NewBodyOperationType.REMOVE, "oppositeDirection" : true, "depth" : 25.4 * mm});
        }
    });
